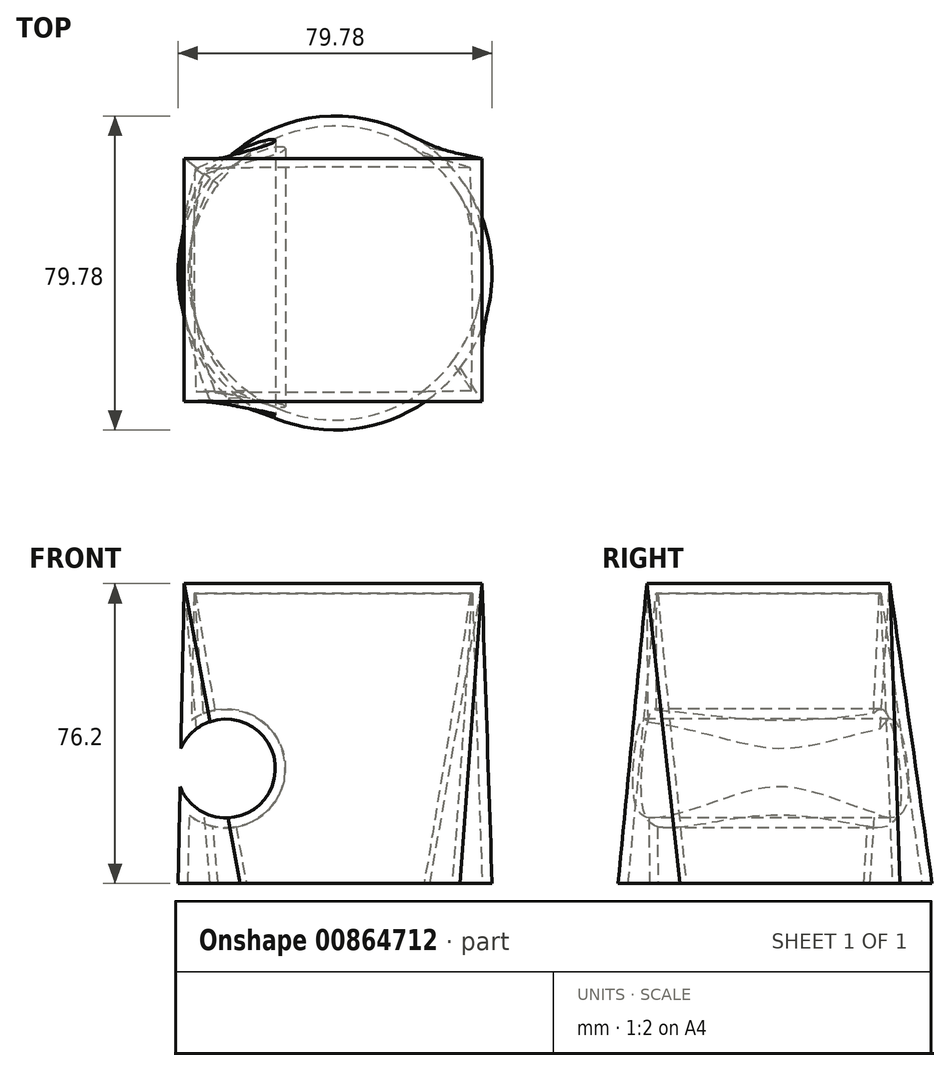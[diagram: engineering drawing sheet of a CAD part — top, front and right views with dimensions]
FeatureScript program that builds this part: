
annotation { "Feature Type Name" : "Feature", "Feature Type Description" : "" }
export const myFeature = defineFeature(function(context is Context, id is Id, definition is map)
    precondition{}
    {
        {
            var Q0;
            Q0=qCreatedBy(makeId("Top.planeOp"),FACE);
            cPlane(context, id + "F0", {"entities" : qUnion([Q0]), "cplaneType" : CPlaneType.OFFSET, "offset" : 76.2 * mm, "width" : 152.4 * mm, "height" : 152.4 * mm});
        }
        {
            var Q0;
            Q0=qCreatedBy(makeId("Top.planeOp"),FACE);
            var sketch = newSketch(context, id + "F1", { "sketchPlane" : qUnion([Q0])});
            skCircle(sketch, "E0", {"center": v(0, 0) * mm, "radius": 39.89 * mm});
            skSolve(sketch);
        }
        {
            var Q0;
            Q0=qCreatedBy(id+"F0.planeOp",FACE);
            var sketch = newSketch(context, id + "F2", { "sketchPlane" : qUnion([Q0])});
            skLineSegment(sketch, "E1.bottom", {"start": v(-38.34, 29.11) * mm, "end": v(37.3, 29.11) * mm});
            skLineSegment(sketch, "E1.top", {"start": v(-38.34, -32.58) * mm, "end": v(37.3, -32.58) * mm});
            skLineSegment(sketch, "E1.left", {"start": v(-38.34, 29.11) * mm, "end": v(-38.34, -32.58) * mm});
            skLineSegment(sketch, "E1.right", {"start": v(37.3, 29.11) * mm, "end": v(37.3, -32.58) * mm});
            skSolve(sketch);
        }
        {
            var Q0;
            Q0=makeQuery(id+"F1.imprint","IMPRINT",FACE,{"disambiguationData":[TD([[makeQuery(id+"F1.imprint","IMPRINT",EDGE,{"derivedFrom":sQuery(id+"F1.wireOp",EDGE,"E0")}),1.0]])]});
            var Q1;
            Q1=makeQuery(id+"F2.imprint","IMPRINT",FACE,{"disambiguationData":[TD([[makeQuery(id+"F2.imprint","IMPRINT",EDGE,{"derivedFrom":sQuery(id+"F2.wireOp",EDGE,"E1.bottom")}),-1.0]])]});
            loft(context, id + "F3", {"sheetProfilesArray" : [{ "sheetProfileEntities" : qUnion([Q0]) }, { "sheetProfileEntities" : qUnion([Q1]) }]});
        }
        {
            var Q0;
            Q0=qCreatedBy(makeId("Front.planeOp"),FACE);
            var sketch = newSketch(context, id + "F4", { "sketchPlane" : qUnion([Q0])});
            skCircle(sketch, "E2", {"center": v(-27.74, 29.22) * mm, "radius": 12.55 * mm});
            skSolve(sketch);
        }
        {
            var Q0;
            Q0=makeQuery(id+"F4.imprint","IMPRINT",FACE,{"disambiguationData":[TD([[makeQuery(id+"F4.imprint","IMPRINT",EDGE,{"derivedFrom":sQuery(id+"F4.wireOp",EDGE,"E2")}),1.0]])]});
            extrude(context, id + "F5", {"entities" : qUnion([Q0]), "operationType" : NewBodyOperationType.REMOVE, "endBound" : BoundingType.SYMMETRIC, "oppositeDirection" : true, "depth" : 76.2 * mm, "offsetDistance" : 25.4 * mm});
        }
        {
            var Q0;
            Q0=makeQuery(id+"F3.opLoft","CAP_FACE",FACE,{"disambiguationData":[OSD([makeQuery(id+"F1.imprint","IMPRINT",FACE,{"disambiguationData":[TD([[makeQuery(id+"F1.imprint","IMPRINT",EDGE,{"derivedFrom":sQuery(id+"F1.wireOp",EDGE,"E0")}),1.0]])]})])],"isStart":true});
            shell(context, id + "F6", {"entities" : qUnion([Q0]), "thickness" : 2.54 * mm});
        }
    });
